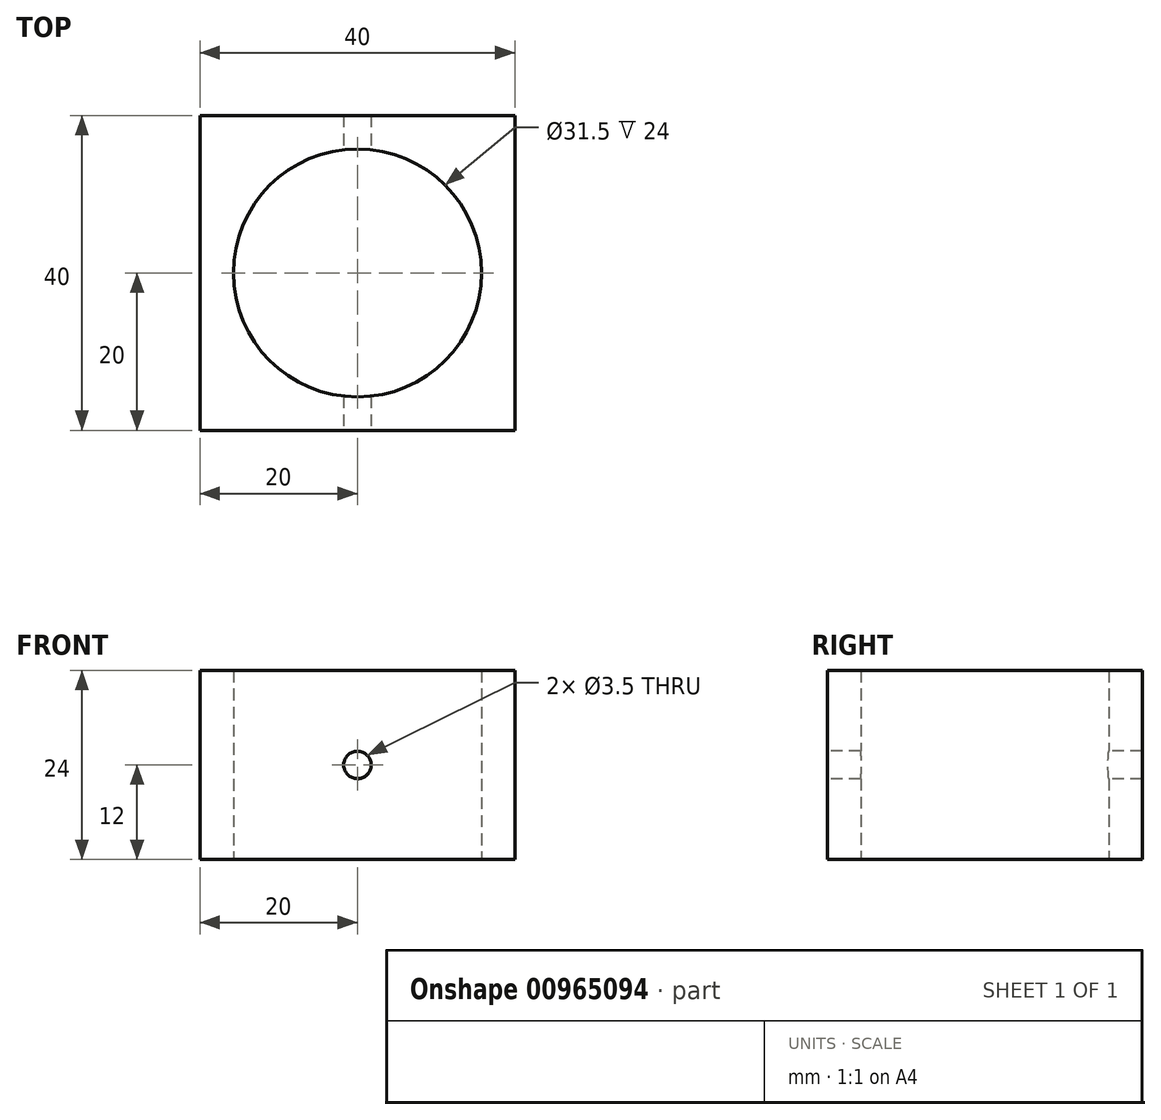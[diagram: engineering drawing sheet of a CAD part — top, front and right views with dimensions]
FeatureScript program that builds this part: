
annotation { "Feature Type Name" : "Feature", "Feature Type Description" : "" }
export const myFeature = defineFeature(function(context is Context, id is Id, definition is map)
    precondition{}
    {
        {
            var Q0;
            Q0=qCreatedBy(makeId("Top.planeOp"),FACE);
            var sketch = newSketch(context, id + "F0", { "sketchPlane" : qUnion([Q0])});
            skLineSegment(sketch, "E0.bottom", {"start": v(0, 0) * mm, "end": v(40, 0) * mm});
            skLineSegment(sketch, "E0.top", {"start": v(0, 40) * mm, "end": v(40, 40) * mm});
            skLineSegment(sketch, "E0.left", {"start": v(0, 0) * mm, "end": v(0, 40) * mm});
            skLineSegment(sketch, "E0.right", {"start": v(40, 0) * mm, "end": v(40, 40) * mm});
            skCircle(sketch, "E1", {"center": v(20, 20) * mm, "radius": 15.75 * mm});
            skSolve(sketch);
        }
        {
            var Q0;
            Q0=makeQuery(id+"F0.imprint","IMPRINT",FACE,{"disambiguationData":[TD([[makeQuery(id+"F0.imprint","IMPRINT",EDGE,{"derivedFrom":sQuery(id+"F0.wireOp",EDGE,"E0.bottom")}),1.0]])]});
            extrude(context, id + "F1", {"entities" : qUnion([Q0]), "depth" : 24 * mm, "offsetDistance" : 25 * mm});
        }
        {
            var Q0;
            Q0=makeQuery(id+"F1.opExtrude","SWEPT_FACE",FACE,{"disambiguationData":[OSD([sQuery(id+"F0.wireOp",EDGE,"E0.bottom")])]});
            var sketch = newSketch(context, id + "F2", { "sketchPlane" : qUnion([Q0])});
            skCircle(sketch, "E2", {"center": v(20, 12) * mm, "radius": 1.75 * mm});
            skSolve(sketch);
        }
        {
            var Q0;
            Q0=makeQuery(id+"F2.imprint","IMPRINT",FACE,{"disambiguationData":[TD([[makeQuery(id+"F2.imprint","IMPRINT",EDGE,{"derivedFrom":sQuery(id+"F2.wireOp",EDGE,"E2")}),1.0]])]});
            extrude(context, id + "F3", {"entities" : qUnion([Q0]), "operationType" : NewBodyOperationType.REMOVE, "oppositeDirection" : true, "depth" : 40 * mm, "offsetDistance" : 25 * mm});
        }
    });
